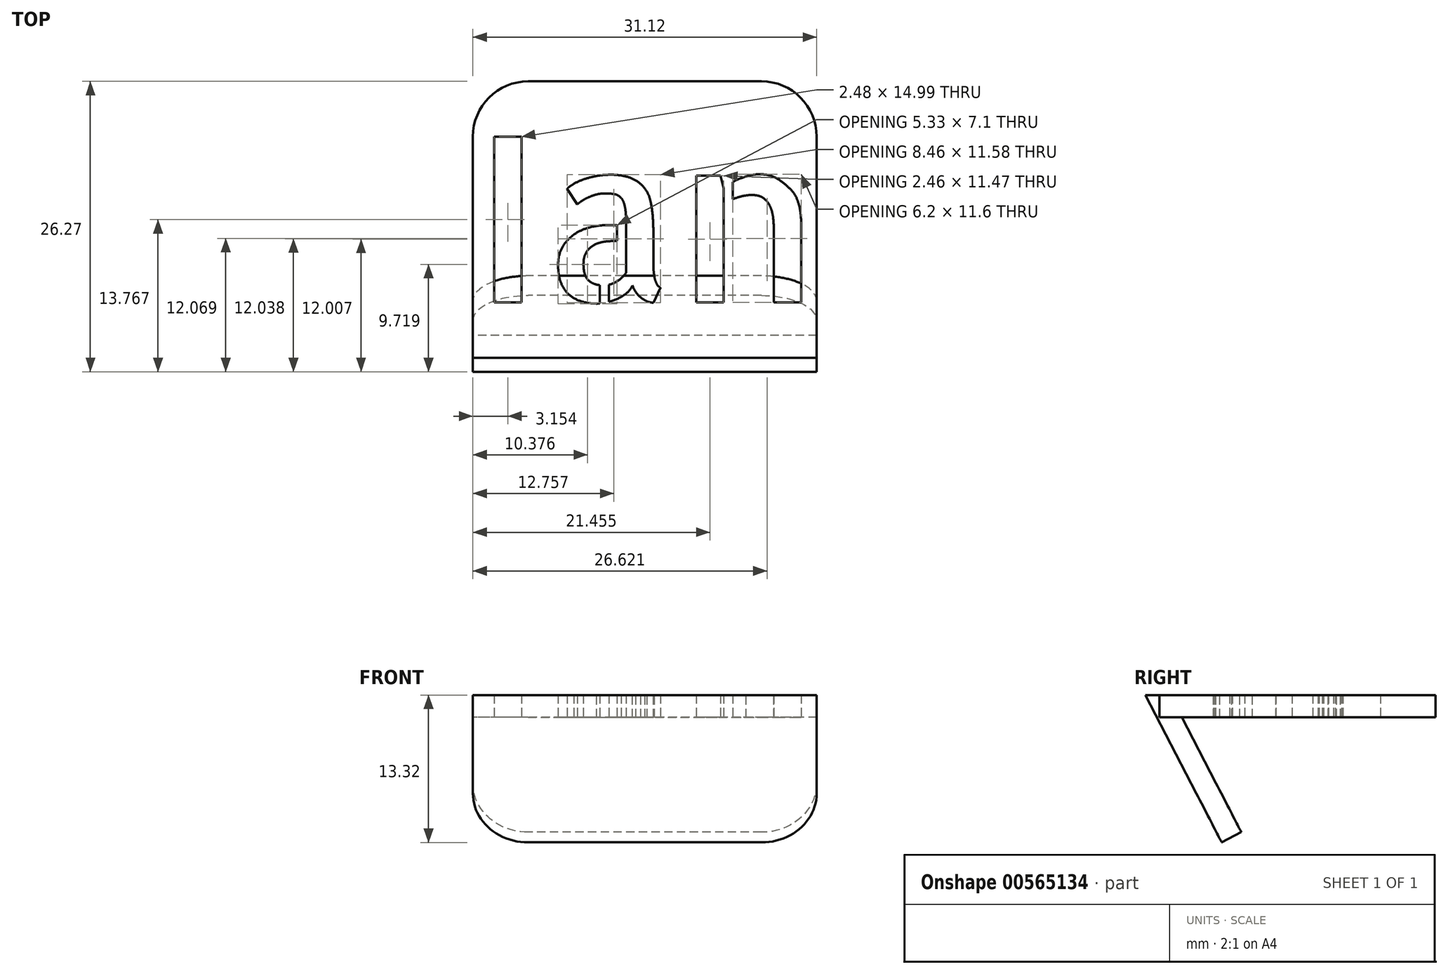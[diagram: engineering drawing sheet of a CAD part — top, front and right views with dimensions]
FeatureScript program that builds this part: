
annotation { "Feature Type Name" : "Feature", "Feature Type Description" : "" }
export const myFeature = defineFeature(function(context is Context, id is Id, definition is map)
    precondition{}
    {
        {
            var Q0;
            Q0=qCreatedBy(makeId("Top.planeOp"),FACE);
            var sketch = newSketch(context, id + "F0", { "sketchPlane" : qUnion([Q0])});
            skLineSegment(sketch, "E0.bottom", {"start": v(-23.58, 12.5) * mm, "end": v(7.54, 12.5) * mm});
            skLineSegment(sketch, "E0.top", {"start": v(-23.58, -12.5) * mm, "end": v(7.54, -12.5) * mm});
            skLineSegment(sketch, "E0.left", {"start": v(-23.58, 12.5) * mm, "end": v(-23.58, -12.5) * mm});
            skLineSegment(sketch, "E0.right", {"start": v(7.54, 12.5) * mm, "end": v(7.54, -12.5) * mm});
            skText(sketch, "E1", { "text": "Ian", "fontName": "AllertaStencil-Regular.ttf"});
            const initialGuessF0  = {"E1": [-0.02358, -0.0075, 1, 0, 0.015]};
            skSetInitialGuess(sketch, initialGuessF0);
            skSolve(sketch);
        }
        {
            var Q0;
            Q0=makeQuery(id+"F0.imprint","IMPRINT",FACE,{"disambiguationData":[TD([[makeQuery(id+"F0.imprint","IMPRINT",EDGE,{"derivedFrom":sQuery(id+"F0.wireOp",EDGE,"E0.bottom")}),-1.0]])]});
            extrude(context, id + "F1", {"entities" : qUnion([Q0]), "depth" : 2 * mm, "offsetDistance" : 25 * mm});
        }
        {
            var Q0;
            {var subQ0=sQuery(id+"F0.wireOp",EDGE,"E0.left");Q0=makeQuery(id+"FYEOEdhl7jzHk82_2.opBoolean","MERGE",FACE,{"derivedFrom":[makeQuery(id+"F1.opExtrude","SWEPT_FACE",FACE,{"disambiguationData":[OSD([subQ0])]}),makeQuery(id+"FOv1BJgTRWeWuMw_1.opExtrude","CAP_FACE",FACE,{"disambiguationData":[OSD([sQuery(id+"F0.wireOp",EDGE,"E0.bottom"),subQ0,sQuery(id+"Fjco5yBOxZZxTCI_1.wireOp",EDGE,"TpTMtmOo-qoIM-rLEy-p7IH-mKgsBanMGF23"),sQuery(id+"Fjco5yBOxZZxTCI_1.wireOp",EDGE,"Ja6BvVoQ-cpFi-Lcom-cL8s-5xC4kZiynyNl"),sQuery(id+"Fjco5yBOxZZxTCI_1.wireOp",EDGE,"utNyaJ8P-FD6r-AD7x-tpFW-fHytfVhziHLl"),sQuery(id+"Fjco5yBOxZZxTCI_1.wireOp",EDGE,"xGzW29bi-H5H8-ObLh-gdKj-mSPkAtMAUUzO")])],"isStart":true})]});}
            var sketch = newSketch(context, id + "F2", { "sketchPlane" : qUnion([Q0])});
            skLineSegment(sketch, "E2", {"start": v(11.52, 2) * mm, "end": v(5.09, -10.4) * mm});
            skLineSegment(sketch, "E3", {"start": v(5.09, -10.4) * mm, "end": v(6.87, -11.32) * mm});
            skLineSegment(sketch, "E4", {"start": v(6.87, -11.32) * mm, "end": v(13.77, 2) * mm});
            skLineSegment(sketch, "E5", {"start": v(13.77, 2) * mm, "end": v(11.52, 2) * mm});
            skSolve(sketch);
        }
        {
            var Q0;
            {var subQ4=sQuery(id+"F2.wireOp",EDGE,"E3");Q0=makeQuery(id+"F2.imprint","IMPRINT",FACE,{"disambiguationData":[TD([[makeQuery(id+"F2.imprint","IMPRINT",EDGE,{"derivedFrom":subQ4}),1.0]])]});}
            var Q1;
            Q1=makeQuery(id+"F1.opExtrude","SWEPT_FACE",FACE,{"disambiguationData":[OSD([sQuery(id+"F0.wireOp",EDGE,"E0.right")])]});
            extrude(context, id + "F3", {"entities" : qUnion([Q0]), "endBound" : BoundingType.UP_TO_SURFACE, "oppositeDirection" : true, "depth" : 75 * mm, "endBoundEntityFace" : qUnion([Q1]), "offsetDistance" : 25 * mm});
        }
        {
            var Q0;
            Q0=makeQuery(id+"F1.opExtrude","SWEPT_EDGE",EDGE,{"disambiguationData":[OSD([sQuery(id+"F0.wireOp",EDGE,"E0.bottom"),sQuery(id+"F0.wireOp",EDGE,"E0.left")])]});
            var Q1;
            Q1=makeQuery(id+"F1.opExtrude","SWEPT_EDGE",EDGE,{"disambiguationData":[OSD([sQuery(id+"F0.wireOp",EDGE,"E0.bottom"),sQuery(id+"F0.wireOp",EDGE,"E0.right")])]});
            var Q2;
            Q2=makeQuery(id+"F3.opExtrude","CAP_EDGE",EDGE,{"disambiguationData":[OSD([sQuery(id+"F2.wireOp",EDGE,"E3")])],"isStart":false});
            var Q3;
            Q3=makeQuery(id+"F3.opExtrude","CAP_EDGE",EDGE,{"disambiguationData":[OSD([sQuery(id+"F2.wireOp",EDGE,"E3")])],"isStart":true});
            var Q4;
            Q4=makeQuery(id+"F3.opExtrude","TWEAK_EDGE",EDGE,{"derivedFrom":[makeQuery(id+"F1.opExtrude","SWEPT_FACE",FACE,{"disambiguationData":[OSD([sQuery(id+"F0.wireOp",EDGE,"E0.right")])]}),makeQuery(id+"F2.imprint","IMPRINT",EDGE,{"derivedFrom":sQuery(id+"F2.wireOp",EDGE,"E3")})]});
            fillet(context, id + "F4", {"entities" : qUnion([Q0, Q1, Q2, Q3, Q4]), "radius" : 5 * mm, "tangentPropagation" : true, "allowEdgeOverflow" : false});
        }
    });
